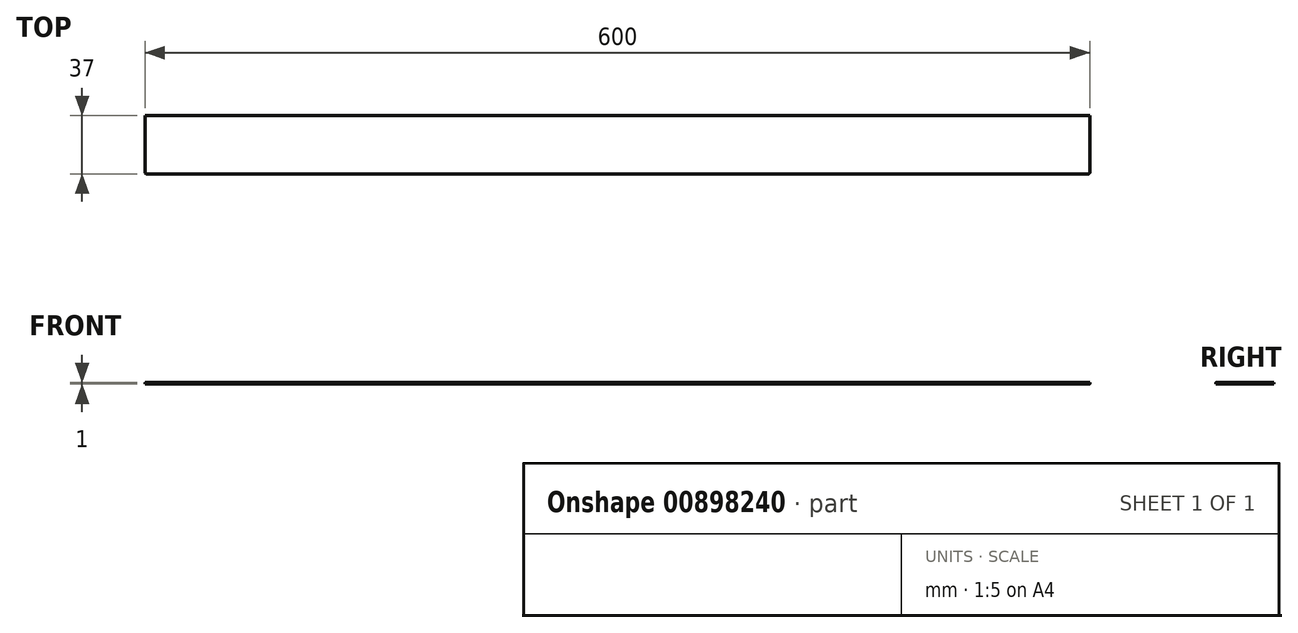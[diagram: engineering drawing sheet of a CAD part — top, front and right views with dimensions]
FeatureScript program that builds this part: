
annotation { "Feature Type Name" : "Feature", "Feature Type Description" : "" }
export const myFeature = defineFeature(function(context is Context, id is Id, definition is map)
    precondition{}
    {
        {
            var Q0;
            Q0=qCreatedBy(makeId("Top.planeOp"),FACE);
            var sketch = newSketch(context, id + "F0", { "sketchPlane" : qUnion([Q0])});
            skLineSegment(sketch, "E0.bottom", {"start": v(299, -18.5) * mm, "end": v(-299, -18.5) * mm});
            skLineSegment(sketch, "E0.top", {"start": v(300, 18.5) * mm, "end": v(-300, 18.5) * mm});
            skLineSegment(sketch, "E0.left", {"start": v(300, -17.5) * mm, "end": v(300, 18.5) * mm});
            skLineSegment(sketch, "E0.right", {"start": v(-300, -17.5) * mm, "end": v(-300, 18.5) * mm});
            skPoint(sketch, "E0.middle", {"position": v(0, 0) * mm});
            skPoint(sketch, "E1.visualSharp", {"position": v(-300, -18.5) * mm});
            skArc(sketch, "E1.filletArc", {"start": v(-300, -17.5) * mm, "mid": v(-299.7, -18.2) * mm, "end": v(-299, -18.5) * mm});
            skPoint(sketch, "E2.visualSharp", {"position": v(300, -18.5) * mm});
            skArc(sketch, "E2.filletArc", {"start": v(299, -18.5) * mm, "mid": v(299.7, -18.2) * mm, "end": v(300, -17.5) * mm});
            skSolve(sketch);
        }
        {
            var Q0;
            Q0=qSketchRegion(id+"F0",true);
            extrude(context, id + "F1", {"entities" : qUnion([Q0]), "depth" : 1 * mm});
        }
    });
